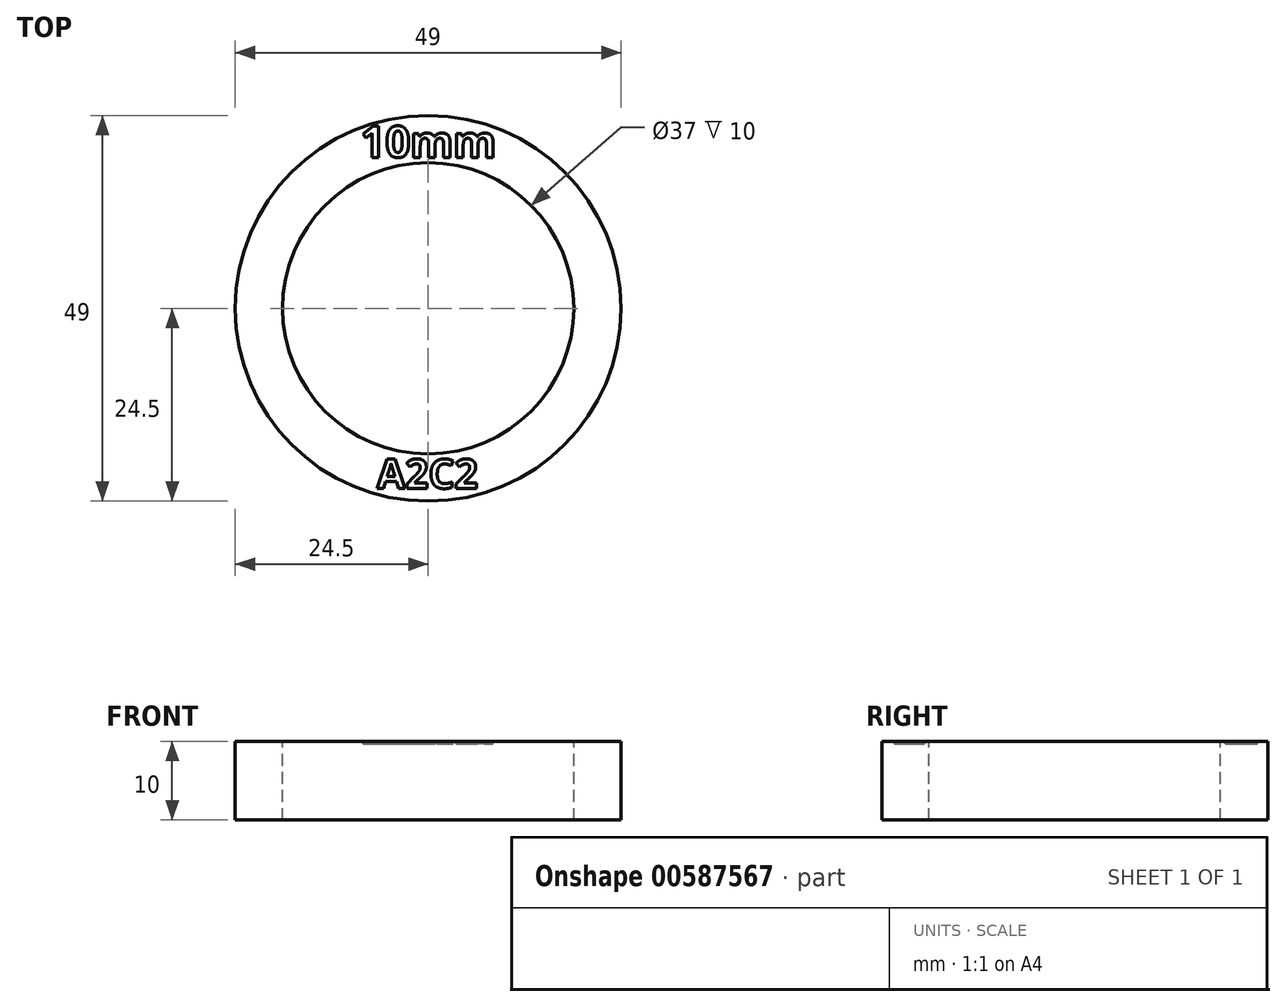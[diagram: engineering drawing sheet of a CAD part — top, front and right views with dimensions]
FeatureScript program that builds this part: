
annotation { "Feature Type Name" : "Feature", "Feature Type Description" : "" }
export const myFeature = defineFeature(function(context is Context, id is Id, definition is map)
    precondition{}
    {
        {
            var Q0;
            Q0=qCreatedBy(makeId("Top.planeOp"),FACE);
            var sketch = newSketch(context, id + "F0", { "sketchPlane" : qUnion([Q0])});
            skCircle(sketch, "E0", {"center": v(0, 0) * mm, "radius": 24.5 * mm});
            skCircle(sketch, "E1", {"center": v(0, 0) * mm, "radius": 18.5 * mm});
            skText(sketch, "E2", { "text": "A2C2", "fontName": "OpenSans-Bold.ttf"});
            skText(sketch, "E3", { "text": "10mm", "fontName": "OpenSans-Bold.ttf"});
            const initialGuessF0  = {"E2": [-0.0065, -0.02287, 1, 0, 0.00374], "E3": [-0.0086, 0.01918, 1, 0, 0.004]};
            skSetInitialGuess(sketch, initialGuessF0);
            skSolve(sketch);
        }
        {
            var Q0;
            Q0 = qSketchRegion(id + "F0", true);
            var Q1;
            Q1=makeQuery(id+"F0.imprint","IMPRINT",FACE,{"disambiguationData":[TD([[makeQuery(id+"F0.imprint","IMPRINT",EDGE,{"derivedFrom":sQuery(id+"F0.wireOp",EDGE,"E2.sketch_text.stroke-0")}),-1.0]])]});
            var Q2;
            Q2=makeQuery(id+"F0.imprint","IMPRINT",FACE,{"disambiguationData":[TD([[makeQuery(id+"F0.imprint","IMPRINT",EDGE,{"derivedFrom":sQuery(id+"F0.wireOp",EDGE,"E2.sketch_text.stroke-8")}),1.0]])]});
            var Q3;
            Q3=makeQuery(id+"F0.imprint","IMPRINT",FACE,{"disambiguationData":[TD([[makeQuery(id+"F0.imprint","IMPRINT",EDGE,{"derivedFrom":sQuery(id+"F0.wireOp",EDGE,"E2.sketch_text.stroke-12")}),-1.0]])]});
            var Q4;
            Q4=makeQuery(id+"F0.imprint","IMPRINT",FACE,{"disambiguationData":[TD([[makeQuery(id+"F0.imprint","IMPRINT",EDGE,{"derivedFrom":sQuery(id+"F0.wireOp",EDGE,"E2.sketch_text.stroke-36")}),-1.0]])]});
            var Q5;
            Q5=makeQuery(id+"F0.imprint","IMPRINT",FACE,{"disambiguationData":[TD([[makeQuery(id+"F0.imprint","IMPRINT",EDGE,{"derivedFrom":sQuery(id+"F0.wireOp",EDGE,"E2.sketch_text.stroke-51")}),-1.0]])]});
            var Q6;
            Q6=makeQuery(id+"F0.imprint","IMPRINT",FACE,{"disambiguationData":[TD([[makeQuery(id+"F0.imprint","IMPRINT",EDGE,{"derivedFrom":sQuery(id+"F0.wireOp",EDGE,"E3.sketch_text.stroke-0")}),-1.0]])]});
            var Q7;
            Q7=makeQuery(id+"F0.imprint","IMPRINT",FACE,{"disambiguationData":[TD([[makeQuery(id+"F0.imprint","IMPRINT",EDGE,{"derivedFrom":sQuery(id+"F0.wireOp",EDGE,"E3.sketch_text.stroke-10")}),-1.0]])]});
            var Q8;
            Q8=makeQuery(id+"F0.imprint","IMPRINT",FACE,{"disambiguationData":[TD([[makeQuery(id+"F0.imprint","IMPRINT",EDGE,{"derivedFrom":sQuery(id+"F0.wireOp",EDGE,"E3.sketch_text.stroke-18")}),1.0]])]});
            var Q9;
            Q9=makeQuery(id+"F0.imprint","IMPRINT",FACE,{"disambiguationData":[TD([[makeQuery(id+"F0.imprint","IMPRINT",EDGE,{"derivedFrom":sQuery(id+"F0.wireOp",EDGE,"E3.sketch_text.stroke-26")}),-1.0]])]});
            var Q10;
            Q10=makeQuery(id+"F0.imprint","IMPRINT",FACE,{"disambiguationData":[TD([[makeQuery(id+"F0.imprint","IMPRINT",EDGE,{"derivedFrom":sQuery(id+"F0.wireOp",EDGE,"E3.sketch_text.stroke-54")}),-1.0]])]});
            extrude(context, id + "F1", {"entities" : qUnion([Q0, Q1, Q2, Q3, Q4, Q5, Q6, Q7, Q8, Q9, Q10]), "oppositeDirection" : true, "depth" : 10 * mm, "offsetDistance" : 25 * mm});
        }
        {
            var Q0;
            Q0=makeQuery(id+"F0.imprint","IMPRINT",FACE,{"disambiguationData":[TD([[makeQuery(id+"F0.imprint","IMPRINT",EDGE,{"derivedFrom":sQuery(id+"F0.wireOp",EDGE,"E2.sketch_text.stroke-12")}),-1.0]])]});
            var Q1;
            Q1=makeQuery(id+"F0.imprint","IMPRINT",FACE,{"disambiguationData":[TD([[makeQuery(id+"F0.imprint","IMPRINT",EDGE,{"derivedFrom":sQuery(id+"F0.wireOp",EDGE,"E2.sketch_text.stroke-0")}),-1.0]])]});
            var Q2;
            Q2=makeQuery(id+"F0.imprint","IMPRINT",FACE,{"disambiguationData":[TD([[makeQuery(id+"F0.imprint","IMPRINT",EDGE,{"derivedFrom":sQuery(id+"F0.wireOp",EDGE,"E2.sketch_text.stroke-36")}),-1.0]])]});
            var Q3;
            Q3=makeQuery(id+"F0.imprint","IMPRINT",FACE,{"disambiguationData":[TD([[makeQuery(id+"F0.imprint","IMPRINT",EDGE,{"derivedFrom":sQuery(id+"F0.wireOp",EDGE,"E2.sketch_text.stroke-51")}),-1.0]])]});
            var Q4;
            Q4=makeQuery(id+"F0.imprint","IMPRINT",FACE,{"disambiguationData":[TD([[makeQuery(id+"F0.imprint","IMPRINT",EDGE,{"derivedFrom":sQuery(id+"F0.wireOp",EDGE,"E3.sketch_text.stroke-0")}),-1.0]])]});
            var Q5;
            Q5=makeQuery(id+"F0.imprint","IMPRINT",FACE,{"disambiguationData":[TD([[makeQuery(id+"F0.imprint","IMPRINT",EDGE,{"derivedFrom":sQuery(id+"F0.wireOp",EDGE,"E3.sketch_text.stroke-10")}),-1.0]])]});
            var Q6;
            Q6=makeQuery(id+"F0.imprint","IMPRINT",FACE,{"disambiguationData":[TD([[makeQuery(id+"F0.imprint","IMPRINT",EDGE,{"derivedFrom":sQuery(id+"F0.wireOp",EDGE,"E3.sketch_text.stroke-26")}),-1.0]])]});
            var Q7;
            Q7=makeQuery(id+"F0.imprint","IMPRINT",FACE,{"disambiguationData":[TD([[makeQuery(id+"F0.imprint","IMPRINT",EDGE,{"derivedFrom":sQuery(id+"F0.wireOp",EDGE,"E3.sketch_text.stroke-54")}),-1.0]])]});
            extrude(context, id + "F2", {"entities" : qUnion([Q0, Q1, Q2, Q3, Q4, Q5, Q6, Q7]), "operationType" : NewBodyOperationType.REMOVE, "oppositeDirection" : true, "depth" : 0.3 * mm, "offsetDistance" : 25 * mm});
        }
    });
